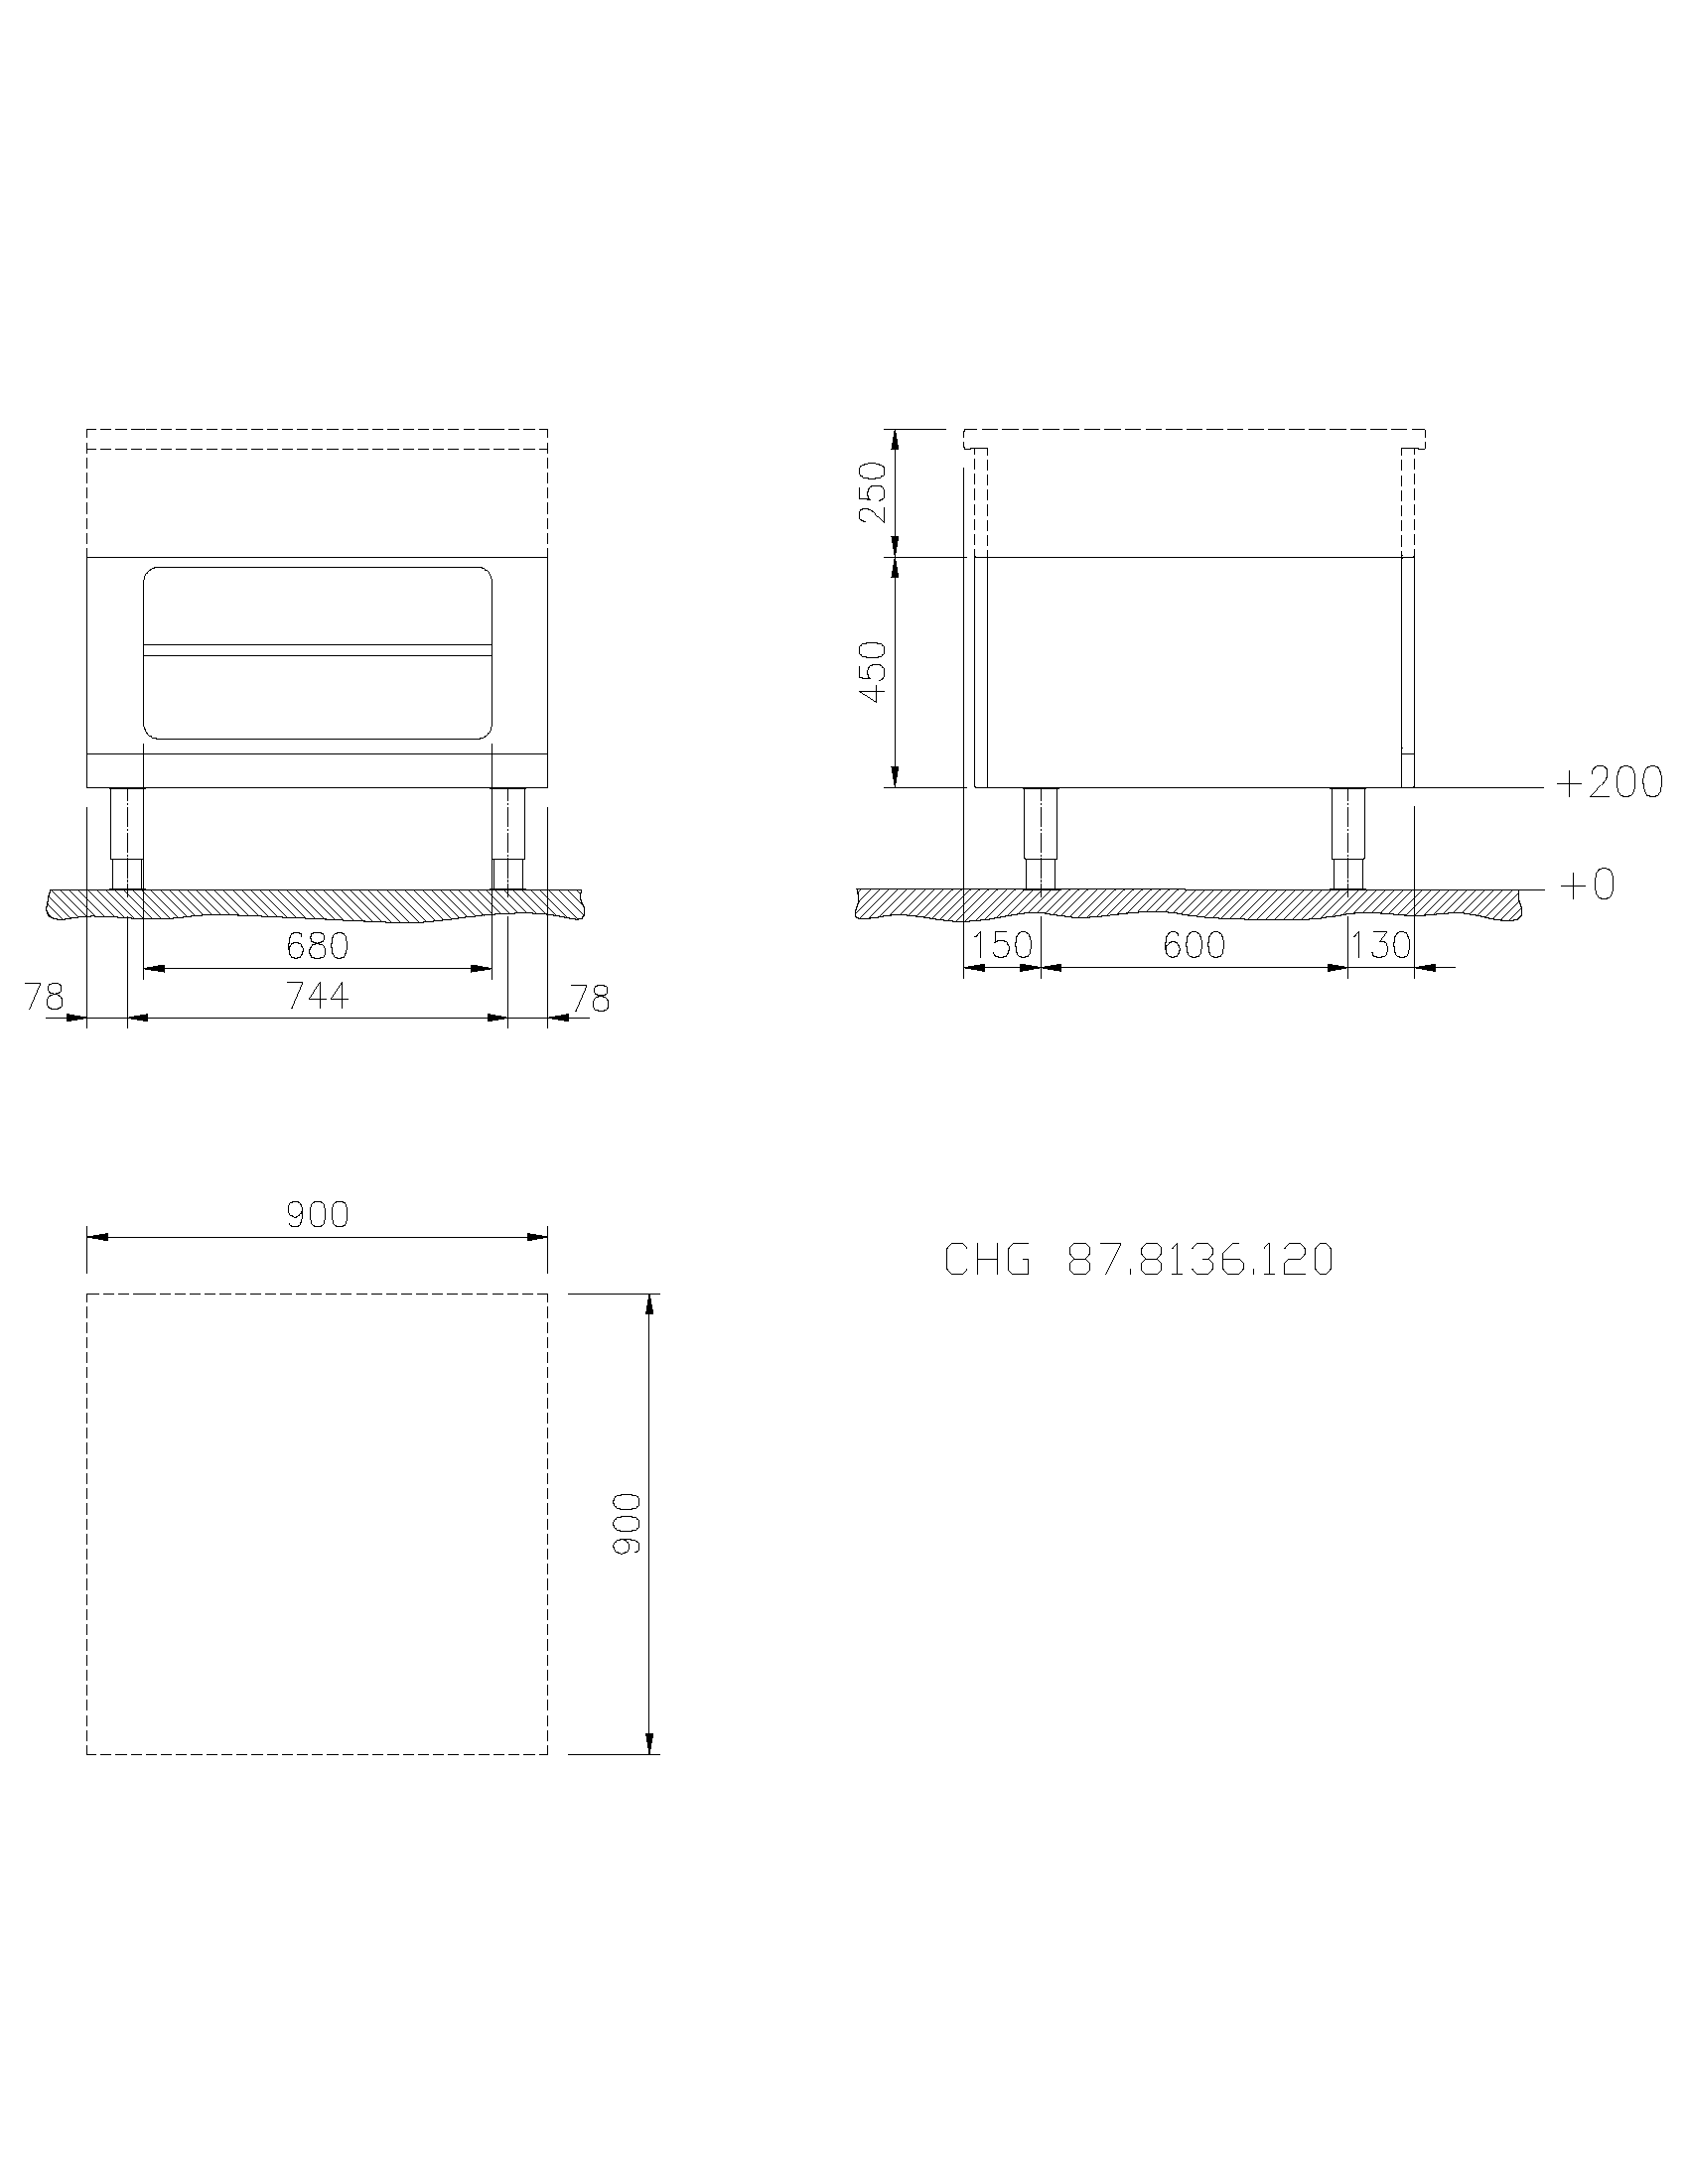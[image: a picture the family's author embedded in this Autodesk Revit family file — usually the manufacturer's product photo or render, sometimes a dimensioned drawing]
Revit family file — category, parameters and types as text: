
# Revit family: QF_ELECTROLUXPROFESSIONAL_589865_MCKCEADDDM
name_source: partatom
category: Specialty Equipment
units: mm (PartAtom-declared; Revit-internal decimal feet)

## family parameters
Always vertical = Yes
Cut with Voids When Loaded = No
Enable Cutting in Views = No
Maintain Annotation Orientation = No
Part Type = Normal
Room Calculation Point = No
Round Connector Dimension = Use Diameter
Shared = No
Work Plane-Based = No

## types (1)
- Standard
    Accessory = Yes
    Cold Water Size = 1"
    Compressed Air Pressure = 0.00 psi
    Compressed Air Size = 0"
    Compressed Air Volume = 0 GPM
    Condensate Return Size = 0"
    Cycle = 50 Hz
    Default Elevation = 0 mm  [stored 0 ft]
    Depth Actual = 900 mm  [stored 2.95276 ft]
    Description = PASTA COOKER, 1X24,5L, 1-SIDE, 400X900X700H-MARINE
    Direct Waste Size = 1"
    Gas Input Pressure = 0.0
    Gas KW = 0
    Gas Size = 0"
    HP = 8 HP
    Height Actual = 700 mm  [stored 2.29659 ft]
    Hot Water Size = 0"
    Item Number = 589865
    Length Actual = 400 mm  [stored 1.31234 ft]
    Manufacturer = Electrolux Professional
    Model = MCKCEADDDM
    Phase = 3
    Refrigerant Compressor Remote = Yes
    Refrigeration Liquid Line Size = 0 mm  [stored 0 ft]
    Refrigeration Suction Line Size = 0 mm  [stored 0 ft]
    Steam Consumption per Hour = 0
    Steam Supply Maximum Pressure = 0.00 psi
    Steam Supply Minimum Pressure = 0.00 psi
    Steam Supply Size = 0"
    URL = https://www.electroluxprofessional.com
    URL Manufacturer = https://www.electroluxprofessional.com
    Volts = 440 V
    Watts = 6000 W
    Weight = 73.00 kg

note: source unit labels omitted for Gas Input Pressure — the stored unit's dimension contradicts the parameter name (converter mislabeling)

note: [stored X ft] marks values corroborated as IEEE doubles in the binary element streams (Revit-internal decimal feet)

## geometry (parser evidence)
native form markers: Blend x4, Sweep x9
no freeform markers — native parametric forms only
